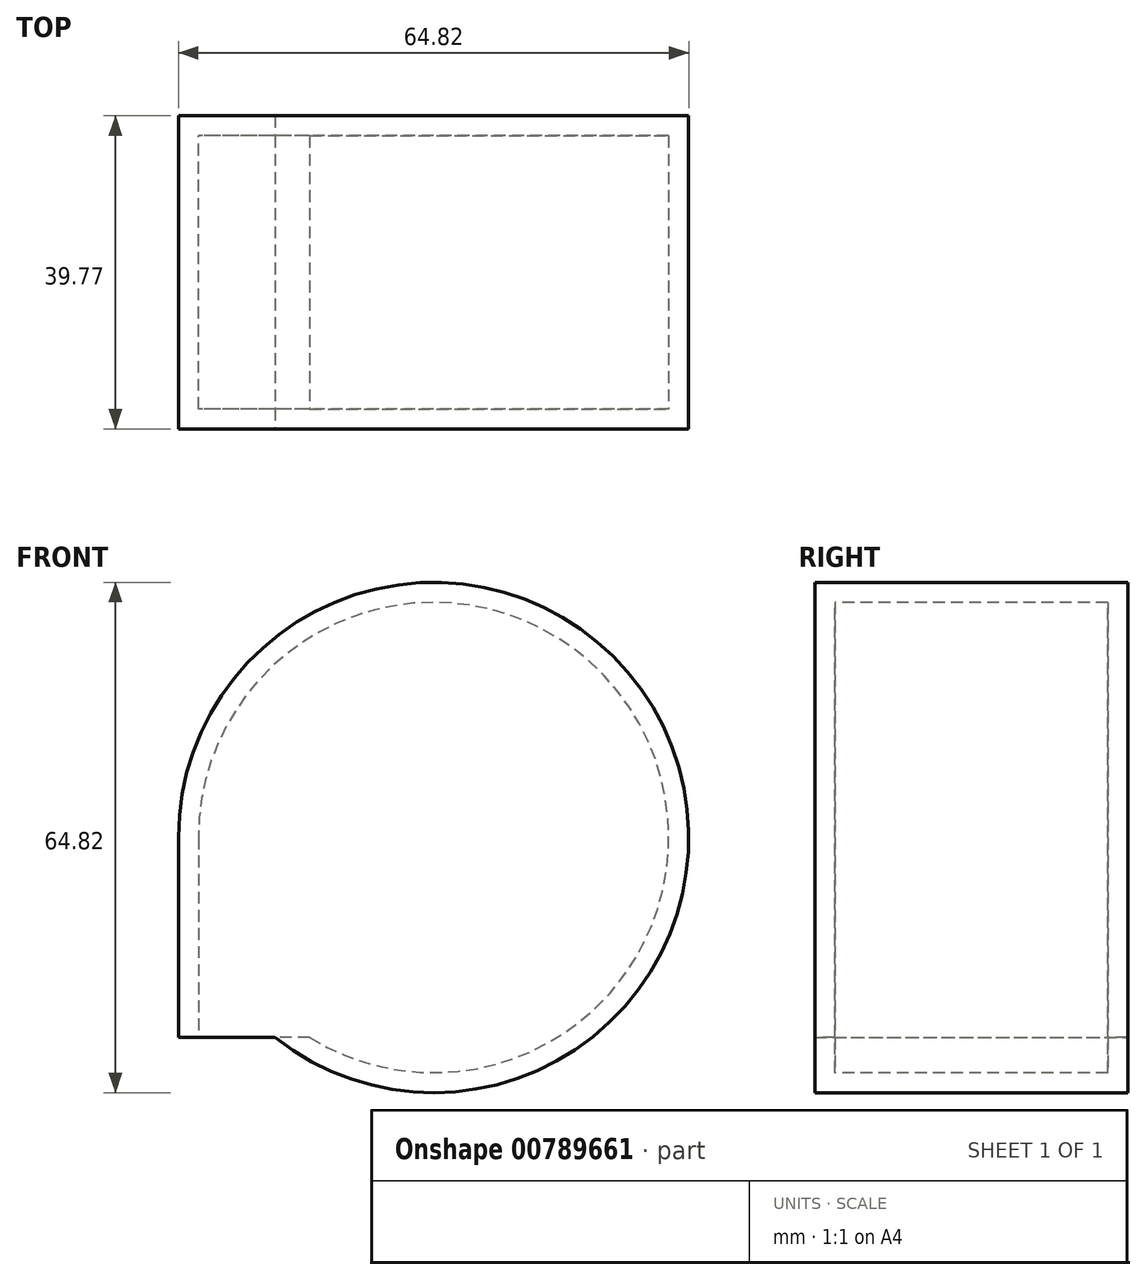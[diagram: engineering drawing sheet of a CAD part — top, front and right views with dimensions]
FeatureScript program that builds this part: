
annotation { "Feature Type Name" : "Feature", "Feature Type Description" : "" }
export const myFeature = defineFeature(function(context is Context, id is Id, definition is map)
    precondition{}
    {
        {
            var Q0;
            Q0=qCreatedBy(makeId("Top.planeOp"),FACE);
            var sketch = newSketch(context, id + "F0", { "sketchPlane" : qUnion([Q0])});
            skLineSegment(sketch, "E0.bottom", {"start": v(18.48, -25.75) * mm, "end": v(-13.93, -25.75) * mm});
            skLineSegment(sketch, "E0.top", {"start": v(18.48, 14.02) * mm, "end": v(-13.93, 14.02) * mm});
            skLineSegment(sketch, "E0.left", {"start": v(18.48, -25.75) * mm, "end": v(18.48, 14.02) * mm});
            skLineSegment(sketch, "E0.right", {"start": v(-13.93, -25.75) * mm, "end": v(-13.93, 14.02) * mm});
            skSolve(sketch);
        }
        {
            var Q0;
            Q0 = qSketchRegion(id + "F0", true);
            extrude(context, id + "F1", {"entities" : qUnion([Q0]), "depth" : 25.4 * mm, "offsetDistance" : 25.4 * mm});
        }
        {
            var Q0;
            Q0=makeQuery(id+"F1.opExtrude","CAP_FACE",FACE,{"disambiguationData":[OSD([sQuery(id+"F0.wireOp",EDGE,"E0.bottom"),sQuery(id+"F0.wireOp",EDGE,"E0.top"),sQuery(id+"F0.wireOp",EDGE,"E0.left"),sQuery(id+"F0.wireOp",EDGE,"E0.right")])],"isStart":false});
            var Q1;
            Q1=makeQuery(id+"F1.opExtrude","CAP_EDGE",EDGE,{"disambiguationData":[OSD([sQuery(id+"F0.wireOp",EDGE,"E0.left")])],"isStart":false});
            revolve(context, id + "F2", {"operationType" : NewBodyOperationType.ADD, "surfaceOperationType" : NewSurfaceOperationType.NEW, "entities" : qUnion([Q0]), "axis" : qUnion([Q1]), "revolveType" : RevolveType.FULL});
        }
        {
            var Q0;
            Q0=makeQuery(id+"F1.opExtrude","CAP_FACE",FACE,{"disambiguationData":[OSD([sQuery(id+"F0.wireOp",EDGE,"E0.bottom"),sQuery(id+"F0.wireOp",EDGE,"E0.top"),sQuery(id+"F0.wireOp",EDGE,"E0.left"),sQuery(id+"F0.wireOp",EDGE,"E0.right")])],"isStart":true});
            shell(context, id + "F3", {"entities" : qUnion([Q0]), "thickness" : 2.54 * mm});
        }
    });
